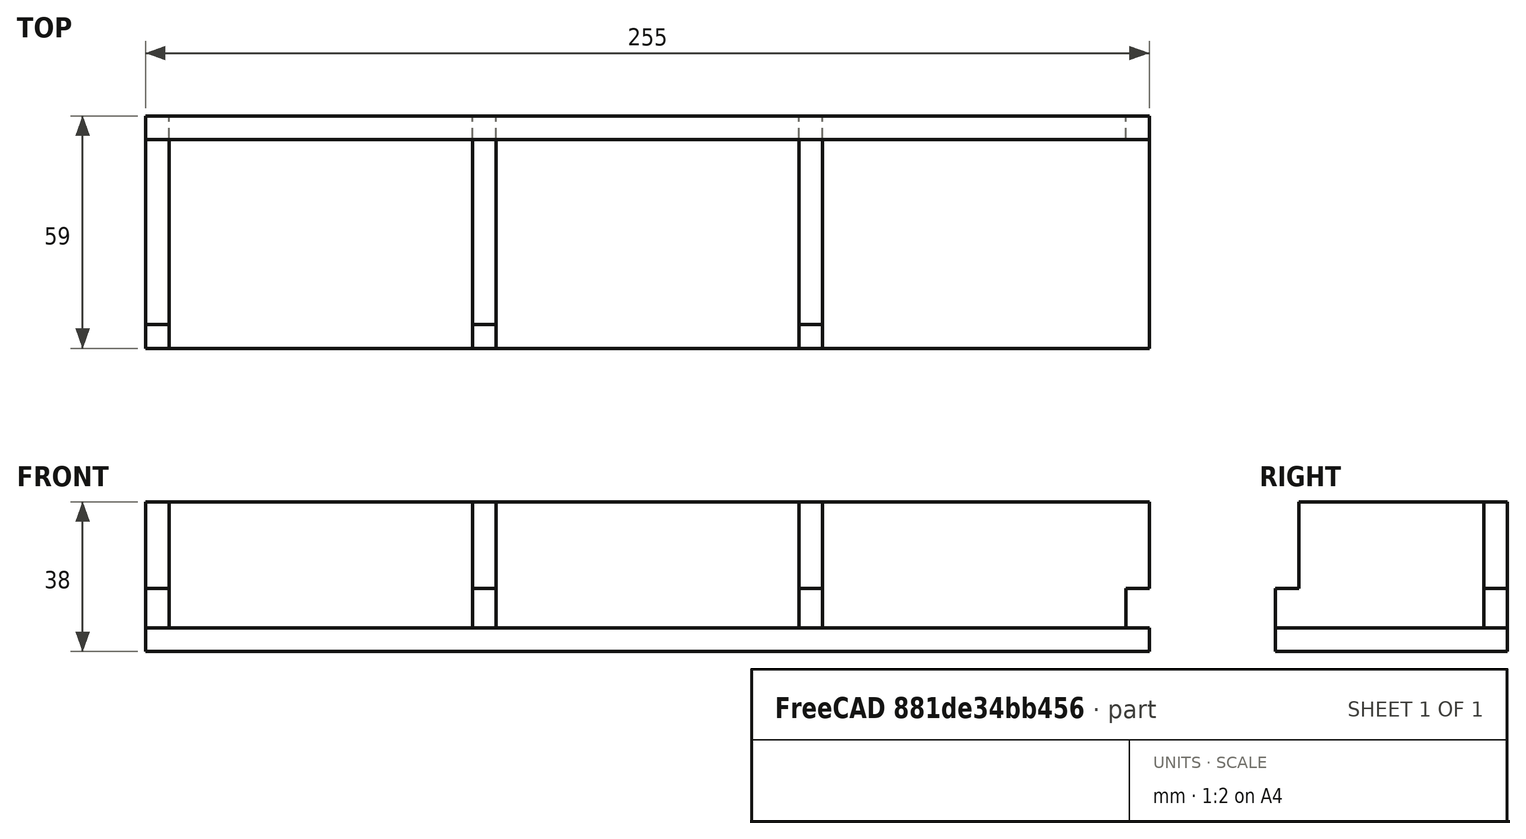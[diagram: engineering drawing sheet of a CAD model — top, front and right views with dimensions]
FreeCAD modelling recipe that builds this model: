
FCSTD DOCUMENT  (FreeCAD 0.18R16146 (Git))
Label: brass birmingham - money tray
License: All rights reserved
LicenseURL: http://en.wikipedia.org/wiki/All_rights_reserved
objects: TechDraw::DrawViewPart×8, PartDesign::Body×7, Sketcher::SketchObject×5, PartDesign::FeatureBase×4, PartDesign::Pad×3, Spreadsheet::Sheet×2, PartDesign::Pocket×2, App::DocumentObjectGroup×2, TechDraw::DrawSVGTemplate×2, TechDraw::DrawViewDimension×2, TechDraw::DrawPage×2
note: 26 computed .brp shape members not serialized (recipe doc carries the construction recipe); baked Part::Feature solids carry a one-line shape summary decoded from their .brp

FEATURE [Spreadsheet::Sheet] Spreadsheet  label="my_variables"
  cells = A1=foam_width; B1(foam_width)==6mm; A2=lower_height; B2(lower_height)==29mm; A3=outer height (minus base); B3(height_adjusted)==38mm - B1; A4=outer long width; B4(width_long)==96mm; A5=outer short width; B5(width_short)==59mm
FEATURE [Sketcher::SketchObject] Sketch
  MapMode = 5
  Support = -> [XY_Plane]
  expr: Constraints[9] = my_variables001.width_short
  expr: Constraints[10] = my_variables001.width_long
  sketch-geometry (4):
    g0: LineSegment StartX=-127.5 StartY=59 StartZ=0 EndX=127.5 EndY=59 EndZ=0
    g1: LineSegment StartX=127.5 StartY=59 StartZ=0 EndX=127.5 EndY=0 EndZ=0
    g2: LineSegment StartX=127.5 StartY=0 StartZ=0 EndX=-127.5 EndY=0 EndZ=0
    g3: LineSegment StartX=-127.5 StartY=0 StartZ=0 EndX=-127.5 EndY=59 EndZ=0
  constraints (11):
    c: Coincident(g0,g1)
    c: Coincident(g1,g2)
    c: Coincident(g2,g3)
    c: Coincident(g3,g0)
    c: Horizontal(g0)
    c: Horizontal(g2)
    c: Vertical(g1)
    c: Vertical(g3)
    c: Symmetric(g2,g2,g-1)
    c: Distance(g3) = 59
    c: Distance(g2) = 255
FEATURE [PartDesign::Pad] Pad
  Length = 6
  Length2 = 100
  Profile = -> Sketch
  Type = 0
  expr: Length = my_variables.foam_width
FEATURE [PartDesign::Body] Body  label="base"
  Group = -> [Sketch,Pad]
  Origin = -> Origin
  Tip = -> Pad
FEATURE [Sketcher::SketchObject] Sketch001
  MapMode = 5
  Placement = pos=(0,0,0) rot=(1,0,0;1.5708rad)
  Support = -> [XZ_Plane001]
  expr: Constraints[10] = my_variables001.width_long
  expr: Constraints[9] = my_variables001.height_adjusted
  sketch-geometry (4):
    g0: LineSegment StartX=-127.5 StartY=32 StartZ=0 EndX=127.5 EndY=32 EndZ=0
    g1: LineSegment StartX=127.5 StartY=32 StartZ=0 EndX=127.5 EndY=0 EndZ=0
    g2: LineSegment StartX=127.5 StartY=0 StartZ=0 EndX=-127.5 EndY=0 EndZ=0
    g3: LineSegment StartX=-127.5 StartY=0 StartZ=0 EndX=-127.5 EndY=32 EndZ=0
  constraints (11):
    c: Coincident(g0,g1)
    c: Coincident(g1,g2)
    c: Coincident(g2,g3)
    c: Coincident(g3,g0)
    c: Horizontal(g0)
    c: Horizontal(g2)
    c: Vertical(g1)
    c: Vertical(g3)
    c: Symmetric(g2,g2,g-1)
    c: Distance(g3) = 32
    c: Distance(g0) = 255
FEATURE [PartDesign::Pad] Pad001
  Length = 6
  Length2 = 100
  Placement = pos=(0,0,0) rot=(1,0,0;1.5708rad)
  Profile = -> Sketch001
  Type = 0
  expr: Length = my_variables.foam_width
FEATURE [Sketcher::SketchObject] Sketch002
  MapMode = 5
  Placement = pos=(0,-6,-1.3e-15) rot=(1,0,0;1.5708rad)
  Support = -> [Pad001]
  expr: Constraints[50] = my_variables001.foam_width
  expr: Constraints[49] = my_variables001.foam_width
  expr: Constraints[30] = my_variables.foam_width
  expr: Constraints[29] = my_variables.foam_width
  expr: Constraints[10] = Sketch001.Constraints[10]
  expr: Constraints[9] = Sketch001.Constraints[9]
  sketch-geometry (20):
    g0: LineSegment [constr] StartX=-127.5 StartY=32 StartZ=0 EndX=127.5 EndY=32 EndZ=0
    g1: LineSegment [constr] StartX=127.5 StartY=32 StartZ=0 EndX=127.5 EndY=0 EndZ=0
    g2: LineSegment [constr] StartX=127.5 StartY=0 StartZ=0 EndX=-127.5 EndY=0 EndZ=0
    g3: LineSegment [constr] StartX=-127.5 StartY=0 StartZ=0 EndX=-127.5 EndY=32 EndZ=0
    g4: LineSegment StartX=-127.5 StartY=10 StartZ=0 EndX=-121.5 EndY=10 EndZ=0
    g5: LineSegment StartX=-121.5 StartY=10 StartZ=0 EndX=-121.5 EndY=0 EndZ=0
    g6: LineSegment StartX=-121.5 StartY=0 StartZ=0 EndX=-127.5 EndY=0 EndZ=0
    g7: LineSegment StartX=-127.5 StartY=0 StartZ=0 EndX=-127.5 EndY=10 EndZ=0
    g8: LineSegment StartX=121.5 StartY=10 StartZ=0 EndX=127.5 EndY=10 EndZ=0
    g9: LineSegment StartX=127.5 StartY=10 StartZ=0 EndX=127.5 EndY=0 EndZ=0
    g10: LineSegment StartX=127.5 StartY=0 StartZ=0 EndX=121.5 EndY=0 EndZ=0
    g11: LineSegment StartX=121.5 StartY=0 StartZ=0 EndX=121.5 EndY=10 EndZ=0
    g12: LineSegment StartX=-44.5 StartY=10 StartZ=0 EndX=-38.5 EndY=10 EndZ=0
    g13: LineSegment StartX=-38.5 StartY=10 StartZ=0 EndX=-38.5 EndY=0 EndZ=0
    g14: LineSegment StartX=-38.5 StartY=0 StartZ=0 EndX=-44.5 EndY=0 EndZ=0
    g15: LineSegment StartX=-44.5 StartY=0 StartZ=0 EndX=-44.5 EndY=10 EndZ=0
    g16: LineSegment StartX=38.5 StartY=10 StartZ=0 EndX=44.5 EndY=10 EndZ=0
    g17: LineSegment StartX=44.5 StartY=10 StartZ=0 EndX=44.5 EndY=0 EndZ=0
    g18: LineSegment StartX=44.5 StartY=0 StartZ=0 EndX=38.5 EndY=0 EndZ=0
    g19: LineSegment StartX=38.5 StartY=0 StartZ=0 EndX=38.5 EndY=10 EndZ=0
  constraints (57):
    c: Coincident(g0,g1)
    c: Coincident(g1,g2)
    c: Coincident(g2,g3)
    c: Coincident(g3,g0)
    c: Horizontal(g0)
    c: Horizontal(g2)
    c: Vertical(g1)
    c: Vertical(g3)
    c: Symmetric(g2,g2,g-1)
    c: Distance(g3) = 32
    c: Distance(g0) = 255
    c: Coincident(g4,g5)
    c: Coincident(g5,g6)
    c: Coincident(g6,g7)
    c: Coincident(g7,g4)
    c: Horizontal(g4)
    c: Horizontal(g6)
    c: Vertical(g5)
    c: Vertical(g7)
    c: Coincident(g8,g9)
    c: Coincident(g9,g10)
    c: Coincident(g10,g11)
    c: Coincident(g11,g8)
    c: Horizontal(g8)
    c: Horizontal(g10)
    c: Vertical(g9)
    c: Vertical(g11)
    c: Coincident(g6,g2)
    c: Coincident(g9,g1)
    c: Distance(g4) = 6
    c: Distance(g8) = 6
    c: Distance(g5) = 10
    c: Distance(g11) = 10
    c: Coincident(g12,g13)
    c: Coincident(g13,g14)
    c: Coincident(g14,g15)
    c: Coincident(g15,g12)
    c: Horizontal(g12)
    c: Horizontal(g14)
    c: Vertical(g13)
    c: Vertical(g15)
    c: Coincident(g16,g17)
    c: Coincident(g17,g18)
    c: Coincident(g18,g19)
    c: Coincident(g19,g16)
    c: Horizontal(g16)
    c: Horizontal(g18)
    c: Vertical(g17)
    c: Vertical(g19)
    c: Distance(g14) = 6
    c: Distance(g18) = 6
    c: PointOnObject(g14,g2)
    c: PointOnObject(g18,g2)
    c: Distance(g15) = 10
    c: Distance(g19) = 10
    c: Distance(g14,g5) = 77
    c: Distance(g18,g13) = 77
FEATURE [PartDesign::Pocket] Pocket
  BaseFeature = -> Pad001
  Length = 5
  Length2 = 100
  Placement = pos=(0,0,0) rot=(1,0,0;1.5708rad)
  Profile = -> Sketch002
  Type = 1
FEATURE [PartDesign::Body] Body001  label="side long"
  Group = -> [Sketch001,Pad001,Sketch002,Pocket]
  Origin = -> Origin001
  Placement = pos=(7e-15,6,6) rot=(0,0,1;0rad)
  Tip = -> Pocket
FEATURE [PartDesign::FeatureBase] Clone
  BaseFeature = -> Body001
  Placement = pos=(7e-15,6,6) rot=(0,0,1;0rad)
FEATURE [PartDesign::Body] Body002  label="side long - clone"
  BaseFeature = -> Body001
  Group = -> [Clone]
  Origin = -> Origin002
  Placement = pos=(7.1e-15,53,-3.2e-14) rot=(0,0,1;0rad)
  Tip = -> Clone
FEATURE [Sketcher::SketchObject] Sketch003
  MapMode = 5
  Placement = pos=(0,0,0) rot=(0.57735,0.57735,0.57735;2.0944rad)
  Support = -> [YZ_Plane003]
  expr: Constraints[10] = my_variables001.width_short
  expr: Constraints[9] = my_variables001.height_adjusted
  sketch-geometry (4):
    g0: LineSegment StartX=-29.5 StartY=32 StartZ=0 EndX=29.5 EndY=32 EndZ=0
    g1: LineSegment StartX=29.5 StartY=32 StartZ=0 EndX=29.5 EndY=0 EndZ=0
    g2: LineSegment StartX=29.5 StartY=0 StartZ=0 EndX=-29.5 EndY=0 EndZ=0
    g3: LineSegment StartX=-29.5 StartY=0 StartZ=0 EndX=-29.5 EndY=32 EndZ=0
  constraints (11):
    c: Coincident(g0,g1)
    c: Coincident(g1,g2)
    c: Coincident(g2,g3)
    c: Coincident(g3,g0)
    c: Horizontal(g0)
    c: Horizontal(g2)
    c: Vertical(g1)
    c: Vertical(g3)
    c: Symmetric(g2,g2,g-1)
    c: Distance(g3) = 32
    c: Distance(g0) = 59
FEATURE [PartDesign::Pad] Pad002
  Length = 6
  Length2 = 100
  Placement = pos=(0,0,0) rot=(0.57735,0.57735,0.57735;2.0944rad)
  Profile = -> Sketch003
  Type = 0
  expr: Length = my_variables.foam_width
FEATURE [Sketcher::SketchObject] Sketch004
  MapMode = 5
  Placement = pos=(6,-2.7e-15,2e-15) rot=(0.57735,0.57735,0.57735;2.0944rad)
  Support = -> [Pad002]
  expr: Constraints[30] = my_variables.foam_width
  expr: Constraints[29] = my_variables.foam_width
  expr: Constraints[10] = Sketch003.Constraints[10]
  expr: Constraints[9] = Sketch003.Constraints[9]
  sketch-geometry (12):
    g0: LineSegment [constr] StartX=-29.5 StartY=32 StartZ=0 EndX=29.5 EndY=32 EndZ=0
    g1: LineSegment [constr] StartX=29.5 StartY=32 StartZ=0 EndX=29.5 EndY=0 EndZ=0
    g2: LineSegment [constr] StartX=29.5 StartY=0 StartZ=0 EndX=-29.5 EndY=0 EndZ=0
    g3: LineSegment [constr] StartX=-29.5 StartY=0 StartZ=0 EndX=-29.5 EndY=32 EndZ=0
    g4: LineSegment StartX=-23.5 StartY=10 StartZ=0 EndX=-29.5 EndY=10 EndZ=0
    g5: LineSegment StartX=-29.5 StartY=10 StartZ=0 EndX=-29.5 EndY=32 EndZ=0
    g6: LineSegment StartX=-29.5 StartY=32 StartZ=0 EndX=-23.5 EndY=32 EndZ=0
    g7: LineSegment StartX=-23.5 StartY=32 StartZ=0 EndX=-23.5 EndY=10 EndZ=0
    g8: LineSegment StartX=23.5 StartY=10 StartZ=0 EndX=29.5 EndY=10 EndZ=0
    g9: LineSegment StartX=29.5 StartY=10 StartZ=0 EndX=29.5 EndY=32 EndZ=0
    g10: LineSegment StartX=29.5 StartY=32 StartZ=0 EndX=23.5 EndY=32 EndZ=0
    g11: LineSegment StartX=23.5 StartY=32 StartZ=0 EndX=23.5 EndY=10 EndZ=0
  constraints (33):
    c: Coincident(g0,g1)
    c: Coincident(g1,g2)
    c: Coincident(g2,g3)
    c: Coincident(g3,g0)
    c: Horizontal(g0)
    c: Horizontal(g2)
    c: Vertical(g1)
    c: Vertical(g3)
    c: Symmetric(g2,g2,g-1)
    c: Distance(g3) = 32
    c: Distance(g0) = 59
    c: Coincident(g4,g5)
    c: Coincident(g5,g6)
    c: Coincident(g6,g7)
    c: Coincident(g7,g4)
    c: Horizontal(g4)
    c: Horizontal(g6)
    c: Vertical(g5)
    c: Vertical(g7)
    c: Coincident(g8,g9)
    c: Coincident(g9,g10)
    c: Coincident(g10,g11)
    c: Coincident(g11,g8)
    c: Horizontal(g8)
    c: Horizontal(g10)
    c: Vertical(g9)
    c: Vertical(g11)
    c: Coincident(g9,g0)
    c: Coincident(g5,g0)
    c: Distance(g4) = 6
    c: Distance(g8) = 6
    c: Distance(g2,g4) = 10
    c: Distance(g1,g8) = 10
FEATURE [PartDesign::Pocket] Pocket001
  BaseFeature = -> Pad002
  Length = 5
  Length2 = 100
  Placement = pos=(0,0,0) rot=(0.57735,0.57735,0.57735;2.0944rad)
  Profile = -> Sketch004
  Type = 1
FEATURE [PartDesign::Body] Body003  label="side short"
  Group = -> [Sketch003,Pad002,Sketch004,Pocket001]
  Origin = -> Origin003
  Placement = pos=(121.5,29.5,6) rot=(0,0,1;0rad)
  Tip = -> Pocket001
FEATURE [App::DocumentObjectGroup] Group  label="parts"
  Group = -> [Body,Body001,Body003]
FEATURE [PartDesign::FeatureBase] Clone001
  BaseFeature = -> Body003
  Placement = pos=(34,25,6) rot=(0,0,1;0rad)
FEATURE [PartDesign::Body] Body004  label="side small - clone"
  BaseFeature = -> Body003
  Group = -> [Clone001]
  Origin = -> Origin004
  Placement = pos=(-161.5,4.5,-1.09e-14) rot=(0,0,1;0rad)
  Tip = -> Clone001
FEATURE [TechDraw::DrawSVGTemplate] Template
  Height = 210
  Orientation = 1
  Width = 297
FEATURE [TechDraw::DrawViewPart] View002
  CoarseView = false
  Direction = (0,0,1)
  Focus = 100
  HardHidden = false
  IsoCount = 0
  IsoHidden = false
  IsoVisible = false
  LockPosition = false
  Perspective = false
  Rotation = 0
  ScaleType = 0
  SeamHidden = false
  SeamVisible = false
  SmoothHidden = false
  SmoothVisible = false
  Source = -> [Body]
  X = 142.817
  Y = 172.384
FEATURE [TechDraw::DrawViewDimension] Dimension
  Arbitrary = false
  FormatSpec = %.2f
  LockPosition = false
  MeasureType = 1
  OverTolerance = 0
  References2D = -> [View002]
  Rotation = 0
  ScaleType = 0
  Type = 0
  UnderTolerance = 0
  X = -138.387
  Y = -1.08247
FEATURE [TechDraw::DrawViewDimension] Dimension001
  Arbitrary = false
  FormatSpec = %.2f
  LockPosition = false
  MeasureType = 1
  OverTolerance = 0
  References2D = -> [View002]
  Rotation = 0
  ScaleType = 0
  Type = 0
  UnderTolerance = 0
  X = -3.24743
  Y = -35.7242
FEATURE [TechDraw::DrawViewPart] View003
  CoarseView = false
  Direction = (0,-1,0)
  Focus = 100
  HardHidden = false
  IsoCount = 0
  IsoHidden = false
  IsoVisible = false
  LockPosition = false
  Perspective = false
  Rotation = 0
  ScaleType = 0
  SeamHidden = false
  SeamVisible = false
  SmoothHidden = false
  SmoothVisible = false
  Source = -> [Body001]
  X = 140.923
  Y = 108.518
FEATURE [Spreadsheet::Sheet] Spreadsheet001  label="my_variables001"
  cells = A1=foam_width; B1(foam_width)==6mm; A3=outer height (minus base); B3(height_adjusted)==38mm - B1; A4=outer long width; B4(width_long)==255mm; A5=outer short width; B5(width_short)==59mm
FEATURE [TechDraw::DrawViewPart] View004
  CoarseView = false
  Direction = (0,-1,0)
  Focus = 100
  HardHidden = false
  IsoCount = 0
  IsoHidden = false
  IsoVisible = false
  LockPosition = false
  Perspective = false
  Rotation = 0
  ScaleType = 0
  SeamHidden = false
  SeamVisible = false
  SmoothHidden = false
  SmoothVisible = false
  Source = -> [Body001]
  X = 139.57
  Y = 69.2784
FEATURE [TechDraw::DrawViewPart] View005
  CoarseView = false
  Direction = (1,0,0)
  Focus = 100
  HardHidden = false
  IsoCount = 0
  IsoHidden = false
  IsoVisible = false
  LockPosition = false
  Perspective = false
  Rotation = 0
  ScaleType = 0
  SeamHidden = false
  SeamVisible = false
  SmoothHidden = false
  SmoothVisible = false
  Source = -> [Body003]
  X = 110.343
  Y = 26.7912
FEATURE [TechDraw::DrawViewPart] View006
  CoarseView = false
  Direction = (1,0,0)
  Focus = 100
  HardHidden = false
  IsoCount = 0
  IsoHidden = false
  IsoVisible = false
  LockPosition = false
  Perspective = false
  Rotation = 0
  ScaleType = 0
  SeamHidden = false
  SeamVisible = false
  SmoothHidden = false
  SmoothVisible = false
  Source = -> [Body003]
  X = 41.8763
  Y = 27.8737
FEATURE [TechDraw::DrawSVGTemplate] Template001
  Height = 210
  Orientation = 1
  Width = 297
FEATURE [PartDesign::FeatureBase] Clone002
  BaseFeature = -> Body003
  Placement = pos=(121.5,29.5,6) rot=(0,0,1;0rad)
FEATURE [PartDesign::Body] Body005  label="side small - divider - clone"
  Group = -> [Clone002]
  Origin = -> Origin005
  Placement = pos=(-166,-1.33e-14,1.07e-14) rot=(0,0,1;0rad)
  Tip = -> Clone002
FEATURE [PartDesign::FeatureBase] Clone003
  BaseFeature = -> Body003
  Placement = pos=(121.5,29.5,6) rot=(0,0,1;0rad)
FEATURE [PartDesign::Body] Body006  label="side small - divder - clone 2"
  Group = -> [Clone003]
  Origin = -> Origin006
  Placement = pos=(-83,-1.33e-14,1.07e-14) rot=(0,0,1;0rad)
  Tip = -> Clone003
FEATURE [App::DocumentObjectGroup] Group001  label="clones"
  Group = -> [Body002,Body004,Body005,Body006]
FEATURE [TechDraw::DrawViewPart] View
  CoarseView = false
  Direction = (0.577,-0.577,0.577)
  Focus = 100
  HardHidden = false
  IsoCount = 0
  IsoHidden = false
  IsoVisible = false
  LockPosition = false
  Perspective = false
  Rotation = 0
  Scale = 1.25
  ScaleType = 0
  SeamHidden = false
  SeamVisible = false
  SmoothHidden = false
  SmoothVisible = false
  Source = -> [Body,Body001,Body002,Body003,Body004,Body006,Body005,Group001]
  X = 148.5
  Y = 105
FEATURE [TechDraw::DrawPage] Page001  label="iso view"
  KeepUpdated = true
  ProjectionType = 0
  Scale = 1.25
  Template = -> Template001
  Views = -> [View]
FEATURE [TechDraw::DrawViewPart] View007
  CoarseView = false
  Direction = (1,0,0)
  Focus = 100
  HardHidden = false
  IsoCount = 0
  IsoHidden = false
  IsoVisible = false
  LockPosition = false
  Perspective = false
  Rotation = 0
  ScaleType = 0
  SeamHidden = false
  SeamVisible = false
  SmoothHidden = false
  SmoothVisible = false
  Source = -> [Body005]
  X = 175.021
  Y = 27.3325
FEATURE [TechDraw::DrawViewPart] View008
  CoarseView = false
  Direction = (1,0,0)
  Focus = 100
  HardHidden = false
  IsoCount = 0
  IsoHidden = false
  IsoVisible = false
  LockPosition = false
  Perspective = false
  Rotation = 0
  ScaleType = 0
  SeamHidden = false
  SeamVisible = false
  SmoothHidden = false
  SmoothVisible = false
  Source = -> [Body006]
  X = 239.157
  Y = 27.8737
FEATURE [TechDraw::DrawPage] Page  label="Parts"
  KeepUpdated = true
  ProjectionType = 0
  Template = -> Template
  Views = -> [View002,Dimension,Dimension001,View003,View004,View005,View006,View007,View008]
